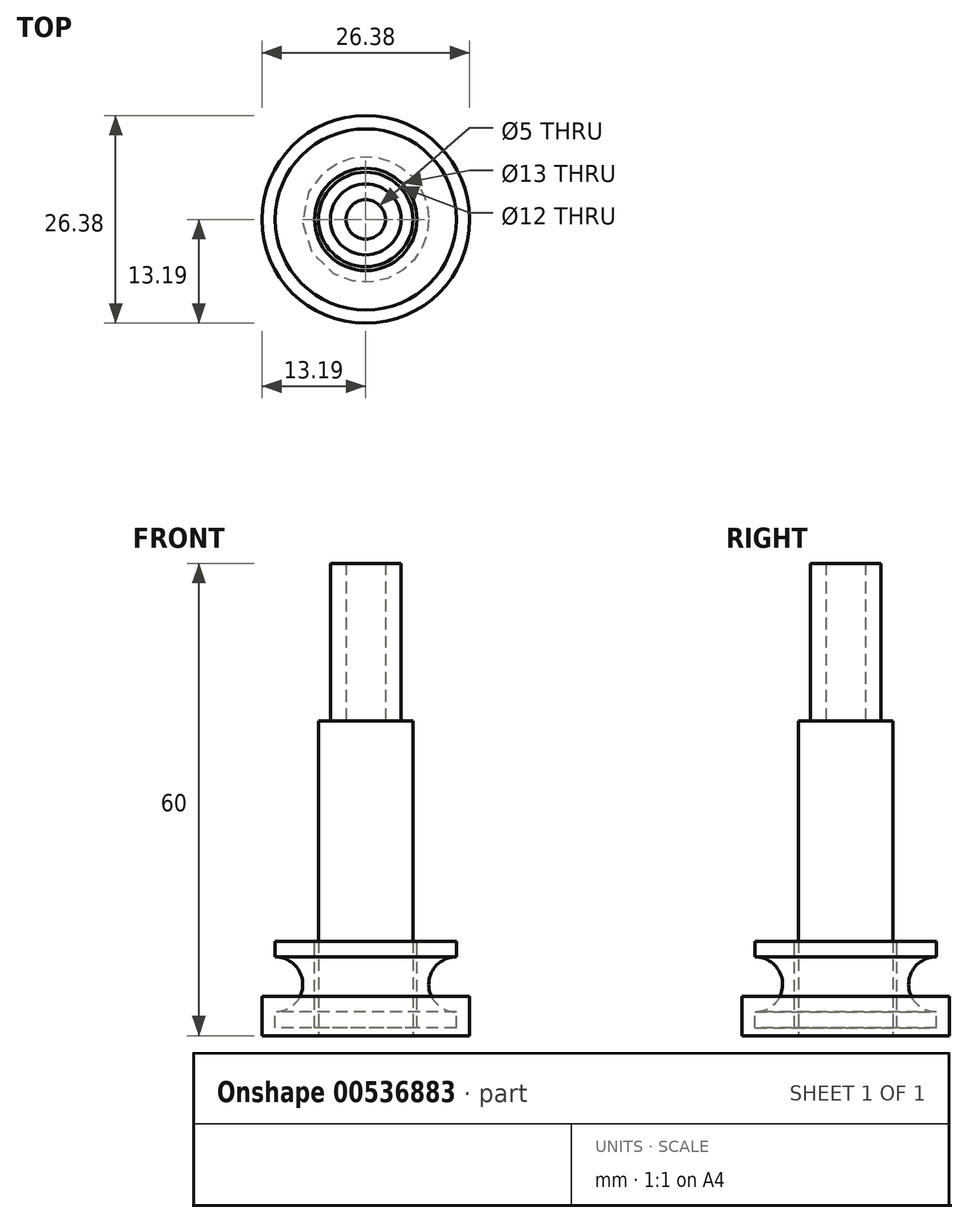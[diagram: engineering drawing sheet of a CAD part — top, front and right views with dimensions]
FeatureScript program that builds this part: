
annotation { "Feature Type Name" : "Feature", "Feature Type Description" : "" }
export const myFeature = defineFeature(function(context is Context, id is Id, definition is map)
    precondition{}
    {
        {
            var Q0;
            Q0=qCreatedBy(makeId("Top.planeOp"),FACE);
            var sketch = newSketch(context, id + "F0", { "sketchPlane" : qUnion([Q0])});
            skCircle(sketch, "E0", {"center": v(0, 0) * mm, "radius": 6 * mm});
            skCircle(sketch, "E1", {"center": v(0, 0) * mm, "radius": 13.2 * mm});
            skSolve(sketch);
        }
        {
            var Q0;
            Q0=makeQuery(id+"F0.imprint","IMPRINT",FACE,{"disambiguationData":[TD([[makeQuery(id+"F0.imprint","IMPRINT",EDGE,{"derivedFrom":sQuery(id+"F0.wireOp",EDGE,"E0")}),1.0]])]});
            extrude(context, id + "F1", {"entities" : qUnion([Q0]), "depth" : 40 * mm, "offsetDistance" : 25 * mm});
        }
        {
            var Q0;
            Q0=makeQuery(id+"F1.opExtrude","CAP_FACE",FACE,{"disambiguationData":[OSD([sQuery(id+"F0.wireOp",EDGE,"E0")])],"isStart":false});
            cPlane(context, id + "F2", {"entities" : qUnion([Q0]), "cplaneType" : CPlaneType.OFFSET, "offset" : 0 * mm, "width" : 150 * mm, "height" : 150 * mm});
        }
        {
            var Q0;
            Q0=qCreatedBy(id+"F2.planeOp",FACE);
            var sketch = newSketch(context, id + "F3", { "sketchPlane" : qUnion([Q0])});
            skCircle(sketch, "E2", {"center": v(0, 0) * mm, "radius": 2.5 * mm});
            skCircle(sketch, "E3", {"center": v(0, 0) * mm, "radius": 4.5 * mm});
            skSolve(sketch);
        }
        {
            var Q0;
            Q0=makeQuery(id+"F3.imprint","IMPRINT",FACE,{"disambiguationData":[TD([[makeQuery(id+"F3.imprint","IMPRINT",EDGE,{"derivedFrom":sQuery(id+"F3.wireOp",EDGE,"E2")}),-1.0]])]});
            var Q1;
            Q1 = qConstructionFilter(qBodyType(qCreatedBy(id + "F3" ,EDGE), BodyType.WIRE), ConstructionObject.NO);
            extrude(context, id + "F4", {"entities" : qUnion([Q0]), "surfaceEntities" : qUnion([Q1]), "depth" : 20 * mm, "offsetDistance" : 25 * mm});
        }
        {
            var Q0;
            Q0=qCreatedBy(makeId("Top.planeOp"),FACE);
            var sketch = newSketch(context, id + "F5", { "sketchPlane" : qUnion([Q0])});
            skCircle(sketch, "E4", {"center": v(0, 0) * mm, "radius": 8 * mm});
            skSolve(sketch);
        }
        {
            var Q0;
            Q0=qCreatedBy(makeId("Right.planeOp"),FACE);
            var sketch = newSketch(context, id + "F6", { "sketchPlane" : qUnion([Q0])});
            skLineSegment(sketch, "E5.0", {"start": v(-7, 0) * mm, "end": v(5, 0) * mm, "construction": true});
            skLineSegment(sketch, "E6.bottom", {"start": v(-6.5, 1) * mm, "end": v(-11.5, 1) * mm});
            skLineSegment(sketch, "E6.top", {"start": v(-6.5, 12) * mm, "end": v(-11.5, 12) * mm});
            skLineSegment(sketch, "E6.left", {"start": v(-6.5, 1) * mm, "end": v(-6.5, 12) * mm});
            skLineSegment(sketch, "E6.right", {"start": v(-11.5, 1) * mm, "end": v(-11.5, 3) * mm});
            skArc(sketch, "E7", {"start": v(-11.5, 3) * mm, "mid": v(-8, 6.5) * mm, "end": v(-11.5, 10) * mm});
            skLineSegment(sketch, "E8.trimOffspring", {"start": v(-11.5, 10) * mm, "end": v(-11.5, 12) * mm});
            skLineSegment(sketch, "E9", {"start": v(-11.5, 10) * mm, "end": v(-11.5, 3) * mm, "construction": true});
            skSolve(sketch);
        }
        {
            var Q0;
            Q0 = qSketchRegion(id + "F6", true);
            var Q1;
            Q1=makeQuery(id+"F1.opExtrude","SWEPT_FACE",FACE,{"disambiguationData":[OSD([sQuery(id+"F0.wireOp",EDGE,"E0")])]});
            revolve(context, id + "F7", {"entities" : qUnion([Q0]), "axis" : qUnion([Q1]), "revolveType" : RevolveType.FULL});
        }
        {
            var Q0;
            Q0=makeQuery(id+"F0.imprint","IMPRINT",FACE,{"disambiguationData":[TD([[makeQuery(id+"F0.imprint","IMPRINT",EDGE,{"derivedFrom":sQuery(id+"F0.wireOp",EDGE,"E0")}),-1.0]])]});
            extrude(context, id + "F8", {"entities" : qUnion([Q0]), "depth" : 5 * mm, "offsetDistance" : 25 * mm});
        }
    });
